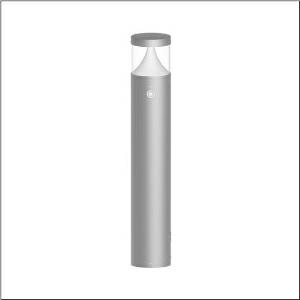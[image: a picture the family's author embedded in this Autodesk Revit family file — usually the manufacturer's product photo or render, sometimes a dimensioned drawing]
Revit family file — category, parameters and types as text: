
# Revit family: cl_31_poller_90_sensor_5cl444803
name_source: partatom
category: Lighting Fixtures
units: mm (PartAtom-declared; Revit-internal decimal feet)

## family parameters
Cut with Voids When Loaded = No
Host = Face
Light Source = No
Part Type = Normal
Room Calculation Point = No
Round Connector Dimension = Use Diameter
Shared = No

## types (1)
- --- (1 x LED, 1500 lm, 14 W, 3000K)
    Apparent Load = 14 VA
    CIE Flux Codes = 19 66 88 92 100
    Color Rendering = 80
    Color Temperature = 3000K
    Default Elevation = 1800 mm
    Description = CL 31 Bollard 90 Sensor, bollard luminaire, primary light control with lens, of PC, primary optical cover: cover panel, of PC, transparent, secondary light control with reflector, of PC, primary light characteristic: asymmetric, LED, rated luminous flux: 1.500lm, luminous efficacy: 107lm/W, light colour: 830, colour temperature: 3000K, control gear: DALI, with terminal, 5-pole, max. 2.5mm², mains connection: 220..240V, AC, 50/60Hz, rated input power: 14W, luminaire housing, of aluminium, powder-coated, Siteco® metallic grey, diameter: 170mm, height: 900mm, PIR sensor, protection rating (complete): IP65, insulation class (complete): insulation class I (protective earthing), certification: CE, ENEC, impact resistance: IK08, permissible operating ambient temperature for outdoor applications: -20..+50°C, packaging unit: 1 piece
    Height = 200 mm  [stored 0.656168 ft]
    Lamp = 1 x LED
    Lamp Light Flux = 1500 lm
    Lamp Power = 14 W
    Lamp count = 1
    Length = 170 mm  [stored 0.557743 ft]
    Luminous efficacy = 107 lm/W
    Manufacturer = Siteco
    ModVariant = No
    Model = 5CL444803
    Mounting Place = Floor
    Mounting Type = Freestanding
    Number of Poles = 1
    OnlyDefault = Yes
    Power Factor = 1
    Product Name = CL 31 Poller 90 Sensor
    Product group = bollard luminaire
    ProductGroupID = 1304
    Protection Class = Protection class I
    Protection Degree = IP 65
    RLX_Detail_Level = 1
    RLX_Emergency_Light_Flux = 0 lm
    RLX_Emergency_Type = 0
    RLX_Emergency_Type_DB = No
    RlxData = <blob elided: 65649 chars, md5=49f83a6f>
    Socket = socket
    Standby Power = 0 W
    System Light Flux = 1500 lm
    System Power = 14 W
    Type Comments = factory setting: luminous flux: 100 % | dim-lin: 254 | 350 mA
    Type Image = l_1006897.jpg
    URL = http://relux.com
    VarID = @adj_195124
    Voltage = 0 V
    Weight = 0.00 kg
    Width = 0 mm  [stored 0 ft]

note: [stored X ft] marks values corroborated as IEEE doubles in the binary element streams (Revit-internal decimal feet)

## geometry (parser evidence)
native form markers: Blend x4, Sweep x11
no freeform markers — native parametric forms only
